# Revit family: Lighting-Industrial-GEWISS-SMART[3]e-WATERTIGHT-LED_TRANSPARENT_800mm
name_source: partatom
category: Apparecchi per illuminazione
units: mm (PartAtom-declared; Revit-internal decimal feet)

## family parameters
Condiviso = No
Host = Superficie
Punto di calcolo locali = Sì
Quota connettore circolare = Usa diametro
Sorgente d'illuminazione = No
Taglio con vuoti quando caricato = No
Tipo di parte = Normale

## types (2) — shared parameters
Application = Internal
Body = Polycarbonate
Catalogue = LIGHTING
Classification: = -
Color Rendering Index = CRI>80
Colour = Grey RAL 7035
Colour : = RAL7035 colored PC paste
Context = Lighting of warehouses, indoor parking and industrial production rooms
Control System = Stand Alone - On / Off
Control System : = ON / OFF
DIN 18032-3 certification = Not available
Device with reduced surface temperature = Yes
Driver = Included
Driver Box = Built-in
Driver failure rate = F10 = 90.000 h a Tq 25°C/F10= 50.000 h a Tq 40°C
Eletrical and lighting features = -
External screw = -
Fixing = Stainless steel support
Ganci = GEWISS  - ALLUMINIO
Gasket = CNC deposited sealant
General information = -
Glow Wire Test : = 850 °C
IDF = 9b64390c-d4e5-4bd6-a395-830a1a5c6723
IDT = c3293776-8468-4c10-80f9-a1d96cfe439a
IP degree = IP66/IP69
IPEA = -
Immagine tipo = GWS3118T.jpg
Installationa and maintenance = -
Insulation class = II
LED Maintenance = Not available
Lampada = LED
Lifetime = L80B20(Tq25°C)=90.000h - L80B20(Tq40°C)=50.000h
Locking Hook = -
Luminaire = LED fixture for general lighting
Lunghezza Lampada = 800 mm  [stored 2.62467 ft]
Materials = -
Maximum surface exposed to the wind : = -
Mouting and installation = Ceiling - Wallmounting - Suspension
Operating temperature : = -25 +40 °C
Optic = Microprismatic transparent
Optic : = Integrated in the screen
Optic Maintenance = Not available
Optic and illuminating features = -
Overvoltage protection = DM 1KV / CM 2KV
Photobiological Risk Class = -
Produttore = GEWISS S.p.A.
Prospetto di default = 1219 mm
Rated frequency (Hz) = 50/60 Hz
Schermo- = Gewiss - Led Acceso
Shield type = UV stabilised polycarbonate
Shock resistance = IK08
Stampa 1_100 = Sì
Stampa 1_200 = No
Standard Deviation Colour Matching = SDCM = 3
Standard- = EN60598-1; IEC 62778; IEC62471
Standards and approvals = -
Stocking temperature = -25 +80 °C
Struttura = GEWISS - SMART 3 - GRIGIO
Supply voltage = 220 - 240 V
Technical sheet = https://www.gewiss.com
Tilt- = With fixing bracket
Type of light source = LED - Not replaceable
URL = https://www.gewiss.com
Unified Glare Rating = -
Unique digital code (Datamatrix) = Datamatrix
Version file RFA = 21.4
Warranty = 5 years
Wiring = With GW connect watertight connector
Wiring : = Stand alone

## per-type parameters (varying)
| type | Descrizione | Modello |
| GWS3120ET840 - SMART3e 800 ON/OFF TRASP CRI80 4000K | SMART3e 800 ON/OFF TRASP CRI80 4000K | GWS3120ET840 |
| GWS3120ET857 - SMART3e 800 ON/OFF TRASP CRI80 5700K | SMART3e 800 ON/OFF TRASP CRI80 5700K | GWS3120ET857 |

note: [stored X ft] marks values corroborated as IEEE doubles in the binary element streams (Revit-internal decimal feet)
